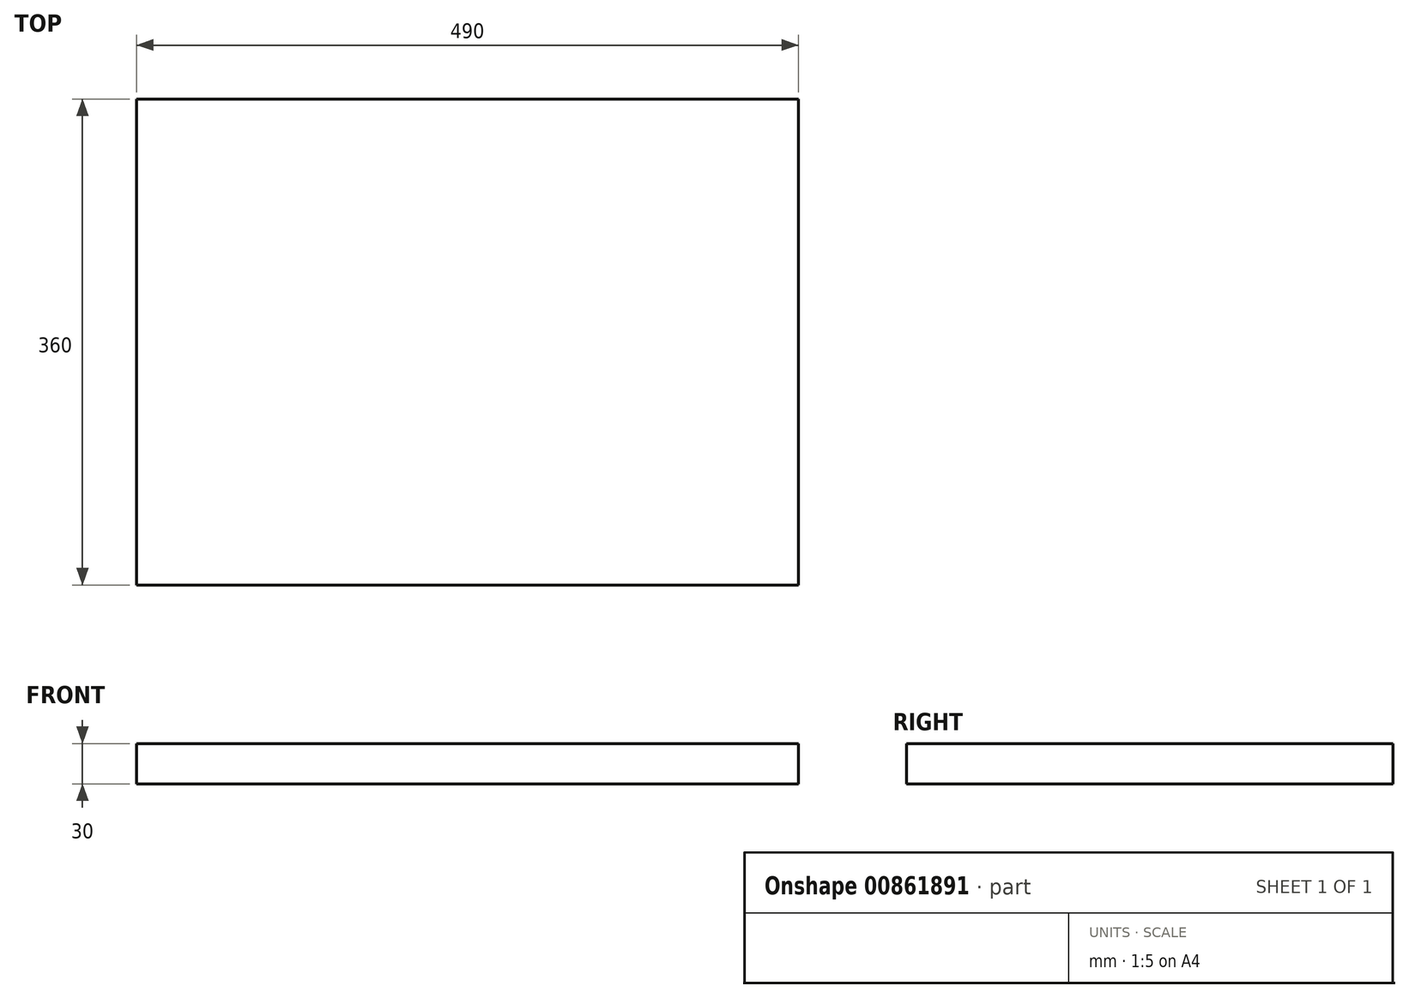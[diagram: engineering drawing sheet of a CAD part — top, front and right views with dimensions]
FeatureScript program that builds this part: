
annotation { "Feature Type Name" : "Feature", "Feature Type Description" : "" }
export const myFeature = defineFeature(function(context is Context, id is Id, definition is map)
    precondition{}
    {
        {
            var Q0;
            Q0=qCreatedBy(makeId("Top.planeOp"),FACE);
            var sketch = newSketch(context, id + "F0", { "sketchPlane" : qUnion([Q0])});
            skLineSegment(sketch, "E0.bottom", {"start": v(-245, -180) * mm, "end": v(245, -180) * mm});
            skLineSegment(sketch, "E0.top", {"start": v(-245, 180) * mm, "end": v(245, 180) * mm});
            skLineSegment(sketch, "E0.left", {"start": v(-245, -180) * mm, "end": v(-245, 180) * mm});
            skLineSegment(sketch, "E0.right", {"start": v(245, -180) * mm, "end": v(245, 180) * mm});
            skPoint(sketch, "E0.middle", {"position": v(0, 0) * mm});
            skSolve(sketch);
        }
        {
            var Q0;
            Q0 = qSketchRegion(id + "F0", true);
            extrude(context, id + "F1", {"entities" : qUnion([Q0]), "depth" : 30 * mm, "offsetDistance" : 25 * mm});
        }
    });
